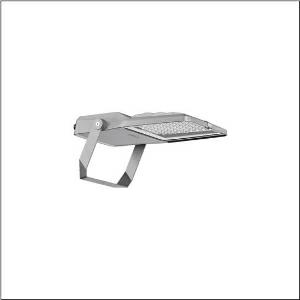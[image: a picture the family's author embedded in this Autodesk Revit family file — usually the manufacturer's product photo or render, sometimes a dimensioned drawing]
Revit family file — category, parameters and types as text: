
# Revit family: floodlight_fl_21_mini___pl64_5xa7772b1e1a_2a70
name_source: partatom
category: Lighting Fixtures
units: mm (PartAtom-declared; Revit-internal decimal feet)

## family parameters
Cut with Voids When Loaded = No
Host = Face
Light Source = No
Part Type = Normal
Room Calculation Point = No
Round Connector Dimension = Use Diameter
Shared = No

## types (1)
- --- (1 x LED, 4990 lm, 45.5 W, 2200K)
    Apparent Load = 46 VA
    CIE Flux Codes = 28 80 98 100 100
    Color Rendering = 70
    Color Temperature = 2200K
    Default Elevation = 1800 mm
    Description = Floodlight FL 21 mini, floodlight, primary light control with lens, of PMMA, primary optical cover: protective disc, of toughened safety glass, transparent, light distribution: PL64, light emission: direct distribution, installation type: surface-mounted, LED, High Power LED, rated luminous flux: 4.990lm, luminous efficacy: 110lm/W, light colour: 722, colour temperature: 2200K, control gear: ECG iQ, control: Street-Remote, Auto-Match, Temp-Guard, Night-Set, Smart-Wire, Desk-Remote (wireless, voltage-free reading and setting of iQ features in the workshop via application-optimized NFC function/RFID function), optimised constant luminous flux control (CLO 2.0), with terminal, 6-pole, mains connection: 220..240V, AC, 50/60Hz, start of lifetime: 46W, end of lifetime: 48W, reduction: 21W, luminaire housing, of diecast aluminium, powder-coated, Siteco® metallic grey (DB 702S), corrosivity category C5 according to DIN EN ISO 12944, mounting bracket, of steel, galvanised, powder-coated, Siteco® metallic grey (DB 702S), protection rating (complete): IP66, insulation class (complete): insulation class II (safety insulation), certification: CE, ENEC, VDE, protection symbol: D, impact resistance: IK08, permissible operating ambient temperature: -40..+40°C, permissible operating ambient temperature for outdoor applications: -40..+50°C, standard: DIN EN 12944, packaging unit: 1 piece

Light Distribution: PL64
    Height = 70 mm
    Lamp = 1 x LED
    Lamp Light Flux = 4990 lm
    Lamp Power = 45.5 W
    Lamp count = 1
    Length = 485 mm
    Luminous efficacy = 110 lm/W
    Manufacturer = Siteco
    ModVariant = No
    Model = 5XA7772B1E1A
    Number of Poles = 1
    OnlyDefault = Yes
    Power Factor = 1
    Product Name = Floodlight FL 21 mini | PL64
    Product group = floodlight | pylon top
    ProductGroupID = 6101
    Protection Class = Protection class II
    Protection Degree = IP 66
    RLX_Detail_Level = 1
    RlxData = <blob elided: 95953 chars, md5=8f026980>
    Socket = socket
    Standby Power = 0 W
    System Light Flux = 4990 lm
    System Power = 46 W
    Type Comments = factory setting: luminous flux: 100 % | dim-lin: 254 | 463 mA
    Type Image = l_1006845.jpg
    URL = http://relux.com
    VarID = @adj_078061
    Voltage = 0 V
    Weight = 0.00 kg
    Width = 337 mm

## geometry (parser evidence)
native form markers: Blend x4, Sweep x12
no freeform markers — native parametric forms only
